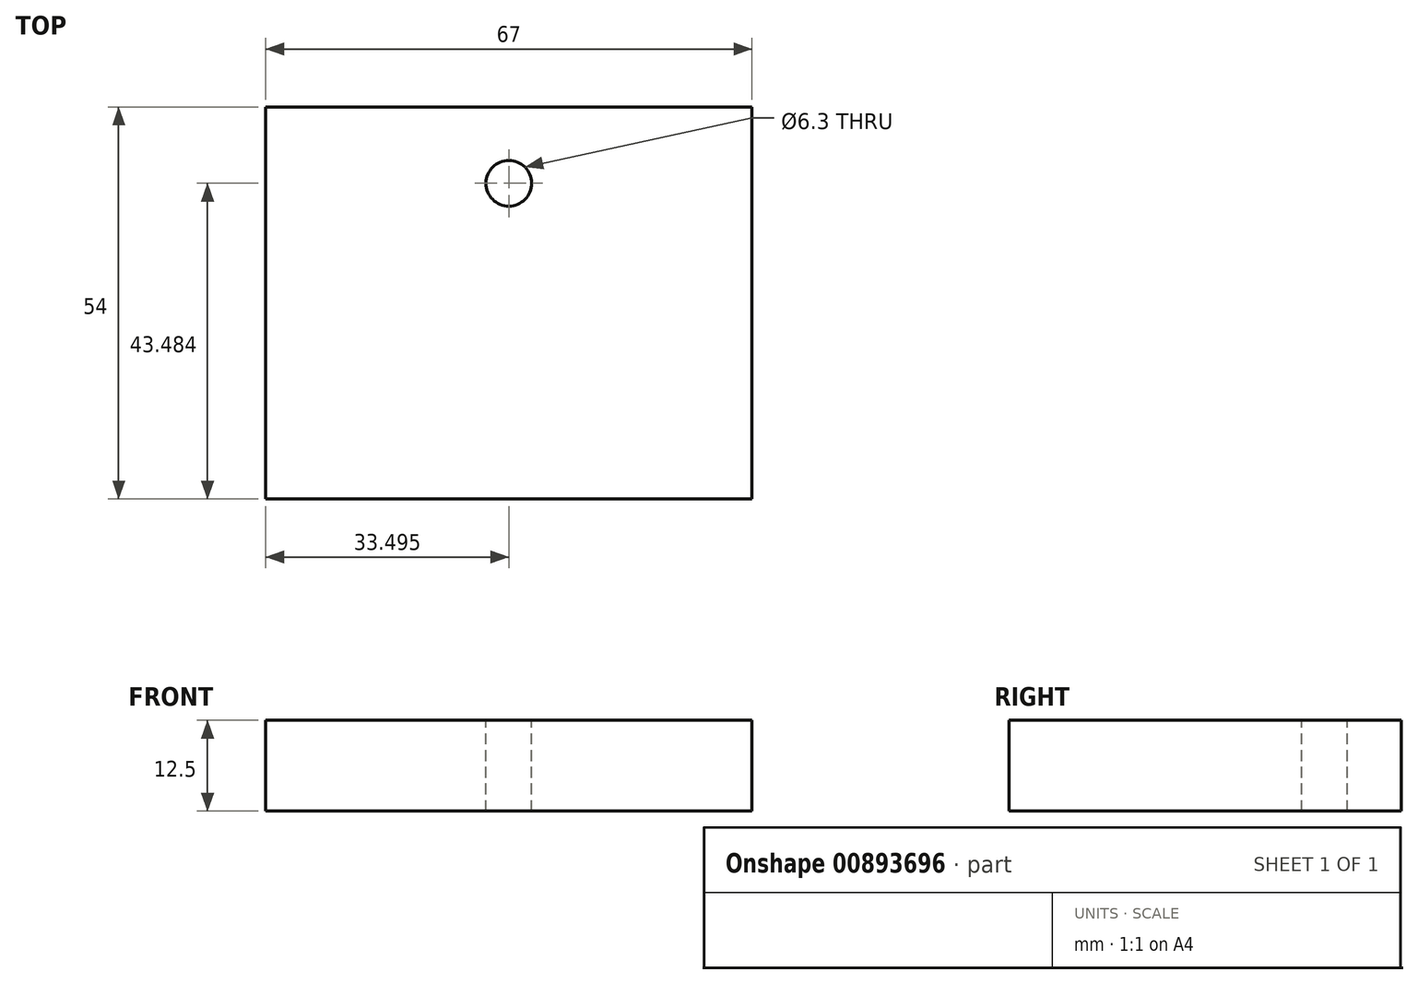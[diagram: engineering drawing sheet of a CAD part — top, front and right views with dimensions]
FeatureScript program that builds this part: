
annotation { "Feature Type Name" : "Feature", "Feature Type Description" : "" }
export const myFeature = defineFeature(function(context is Context, id is Id, definition is map)
    precondition{}
    {
        {
            var Q0;
            Q0=qCreatedBy(makeId("Top.planeOp"),FACE);
            var sketch = newSketch(context, id + "F0", { "sketchPlane" : qUnion([Q0])});
            skLineSegment(sketch, "E0.bottom", {"start": v(-28.56, -26.32) * mm, "end": v(38.44, -26.32) * mm});
            skLineSegment(sketch, "E0.top", {"start": v(-28.56, 27.68) * mm, "end": v(38.44, 27.68) * mm});
            skLineSegment(sketch, "E0.left", {"start": v(-28.56, -26.32) * mm, "end": v(-28.56, 27.68) * mm});
            skLineSegment(sketch, "E0.right", {"start": v(38.44, -26.32) * mm, "end": v(38.44, 27.68) * mm});
            skCircle(sketch, "E1", {"center": v(4.94, 17.16) * mm, "radius": 3.15 * mm});
            skSolve(sketch);
        }
        {
            var Q0;
            Q0 = qSketchRegion(id + "F0", true);
            extrude(context, id + "F1", {"entities" : qUnion([Q0]), "depth" : -12.5 * mm, "offsetDistance" : 25 * mm});
        }
    });
